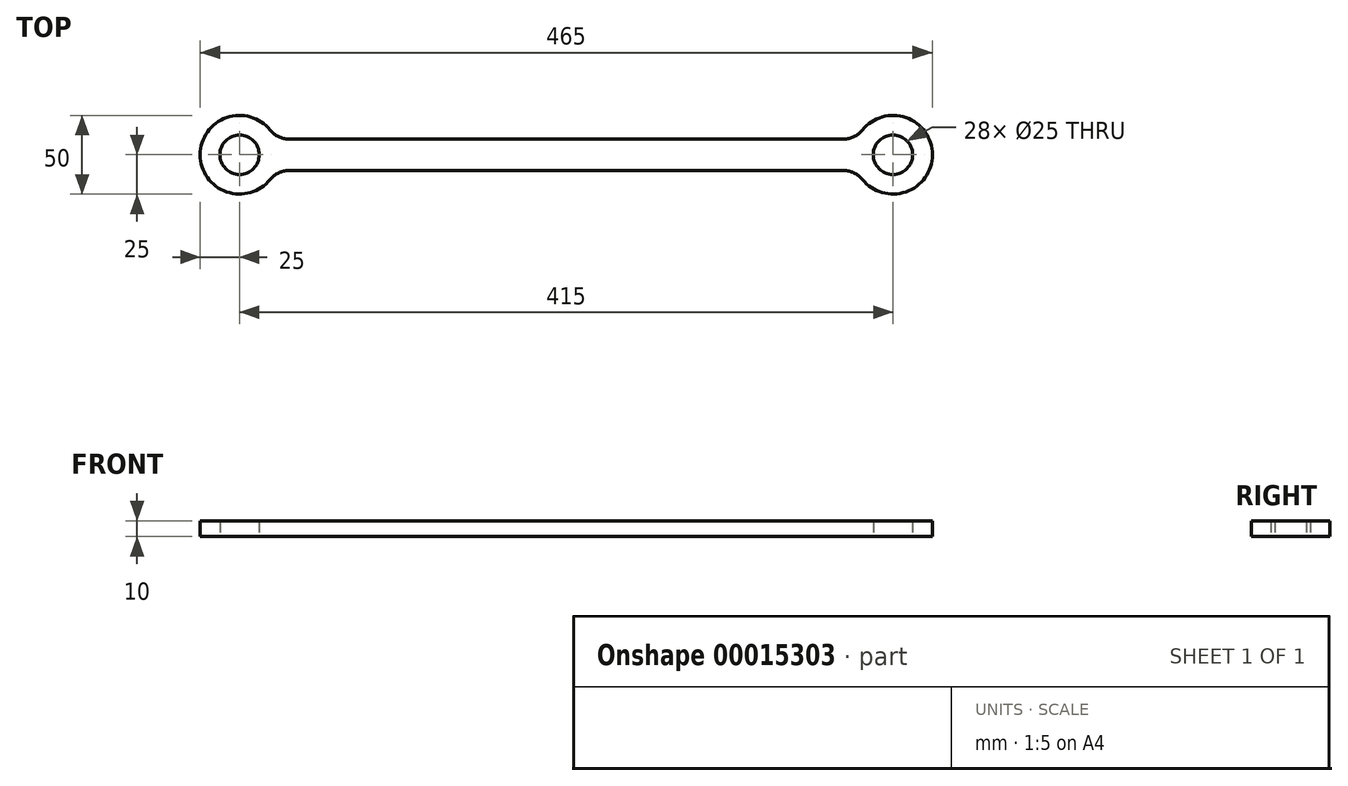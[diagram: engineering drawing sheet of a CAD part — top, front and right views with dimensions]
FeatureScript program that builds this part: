
annotation { "Feature Type Name" : "Feature", "Feature Type Description" : "" }
export const myFeature = defineFeature(function(context is Context, id is Id, definition is map)
    precondition{}
    {
        {
            var Q0;
            Q0=qCreatedBy(makeId("Top.planeOp"),FACE);
            var sketch = newSketch(context, id + "F0", { "sketchPlane" : qUnion([Q0])});
            skArc(sketch, "E0", {"start": v(19.52, 15.63) * mm, "mid": v(-25, 0) * mm, "end": v(19.52, -15.63) * mm});
            skArc(sketch, "E1", {"start": v(395.48, -15.63) * mm, "mid": v(440, 0) * mm, "end": v(395.48, 15.63) * mm});
            skLineSegment(sketch, "E2", {"start": v(31.22, 10) * mm, "end": v(383.78, 10) * mm});
            skLineSegment(sketch, "E3", {"start": v(0, 0) * mm, "end": v(415, 0) * mm, "construction": true});
            skLineSegment(sketch, "E4.MirrorCS", {"start": v(31.22, -10) * mm, "end": v(383.78, -10) * mm});
            skPoint(sketch, "E5.visualSharp", {"position": v(22.91, 10) * mm});
            skArc(sketch, "E5.filletArc", {"start": v(19.52, 15.62) * mm, "mid": v(24.73, 11.48) * mm, "end": v(31.22, 10) * mm});
            skPoint(sketch, "E6.visualSharp", {"position": v(22.91, -10) * mm});
            skArc(sketch, "E6.filletArc", {"start": v(31.22, -10) * mm, "mid": v(24.73, -11.48) * mm, "end": v(19.52, -15.62) * mm});
            skPoint(sketch, "E7.visualSharp", {"position": v(392.09, -10) * mm});
            skArc(sketch, "E7.filletArc", {"start": v(395.48, -15.63) * mm, "mid": v(390.27, -11.48) * mm, "end": v(383.78, -10) * mm});
            skPoint(sketch, "E8.visualSharp", {"position": v(392.09, 10) * mm});
            skArc(sketch, "E8.filletArc", {"start": v(383.78, 10) * mm, "mid": v(390.27, 11.48) * mm, "end": v(395.48, 15.63) * mm});
            skCircle(sketch, "E9", {"center": v(0, 0) * mm, "radius": 12.5 * mm});
            skCircle(sketch, "E10", {"center": v(415, 0) * mm, "radius": 12.5 * mm});
            skSolve(sketch);
        }
        {
            var Q0;
            Q0=qSketchRegion(id+"F0",true);
            extrude(context, id + "F1", {"entities" : qUnion([Q0]), "depth" : 10 * mm});
        }
    });
